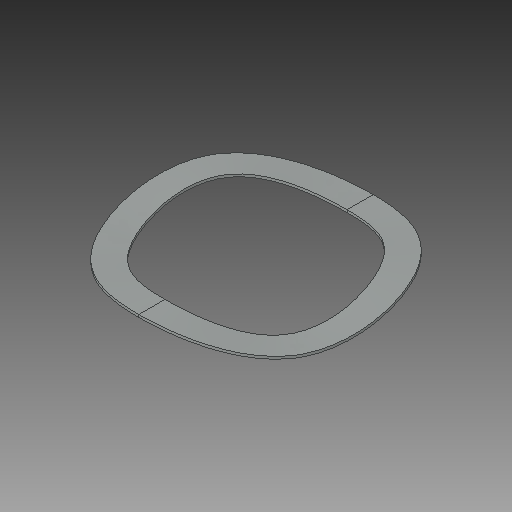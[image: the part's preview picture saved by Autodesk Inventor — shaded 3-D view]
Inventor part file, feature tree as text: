
AUTODESK INVENTOR PART (.ipt)
format: ipt  version: 2017 (Build 210142000, 142)  size: 123,392 bytes
history: native  units: in
note: dims shown in document units (in); Inventor stores cm internally (conversion verified against a paired STEP export)
features: loft x1
ambient origin geometry x8: Origin, YZ Plane, XZ Plane, XY Plane, X Axis, Y Axis, Z Axis, Center Point
bodies: Solid1 (feature_tree)
feature tree (1):
  loft  "Loft1"
